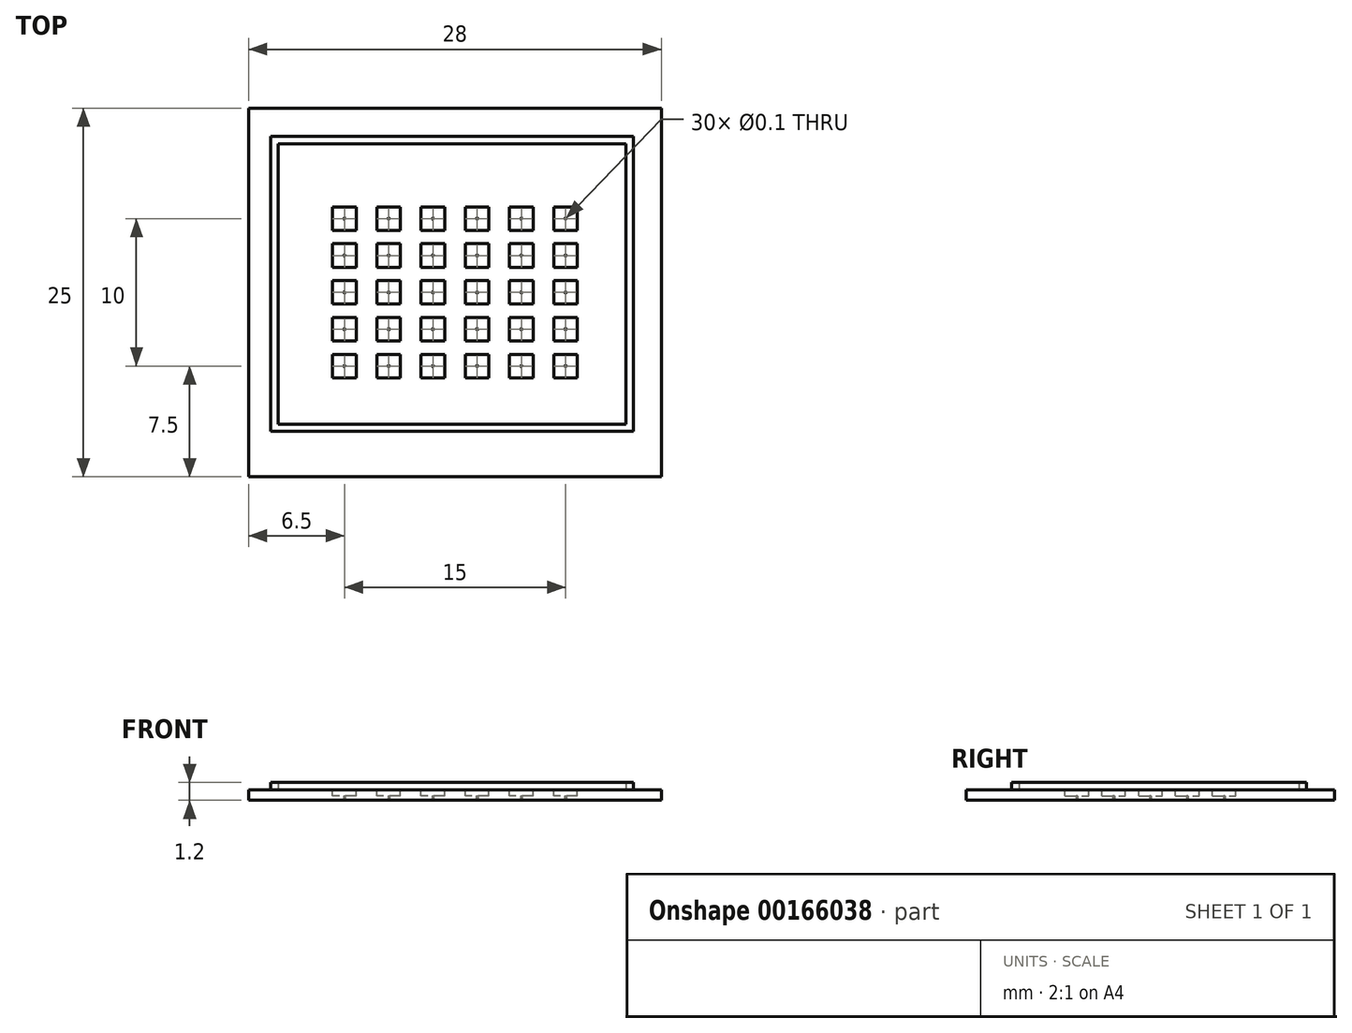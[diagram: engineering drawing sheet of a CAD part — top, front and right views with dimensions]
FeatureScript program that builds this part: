
annotation { "Feature Type Name" : "Feature", "Feature Type Description" : "" }
export const myFeature = defineFeature(function(context is Context, id is Id, definition is map)
    precondition{}
    {
        {
            var Q0;
            Q0=qCreatedBy(makeId("Top.planeOp"),FACE);
            var sketch = newSketch(context, id + "F0", { "sketchPlane" : qUnion([Q0])});
            skLineSegment(sketch, "E0.bottom", {"start": v(14, -12.5) * mm, "end": v(-14, -12.5) * mm});
            skLineSegment(sketch, "E0.top", {"start": v(14, 12.5) * mm, "end": v(-14, 12.5) * mm});
            skLineSegment(sketch, "E0.left", {"start": v(14, -12.5) * mm, "end": v(14, 12.5) * mm});
            skLineSegment(sketch, "E0.right", {"start": v(-14, -12.5) * mm, "end": v(-14, 12.5) * mm});
            skPoint(sketch, "E0.middle", {"position": v(0, 0) * mm});
            skSolve(sketch);
        }
        {
            var Q0;
            Q0=qSketchRegion(id+"F0",true);
            var Q1;
            Q1=makeQuery(id+"F0.imprint","IMPRINT",FACE,{"disambiguationData":[TD([[makeQuery(id+"F0.imprint","IMPRINT",EDGE,{"derivedFrom":sQuery(id+"F0.wireOp",EDGE,"UkhYZKIQ-UkVG-Lxvr-Lrxv-xQsFVOTcTfzZ.bottom")}),-1.0]])]});
            extrude(context, id + "F1", {"entities" : qUnion([Q0, Q1]), "oppositeDirection" : true, "depth" : 0.7 * mm});
        }
        {
            var Q0;
            Q0=makeQuery(id+"F1.opExtrude","CAP_FACE",FACE,{"disambiguationData":[OSD([sQuery(id+"F0.wireOp",EDGE,"E0.bottom"),sQuery(id+"F0.wireOp",EDGE,"E0.top"),sQuery(id+"F0.wireOp",EDGE,"E0.left"),sQuery(id+"F0.wireOp",EDGE,"E0.right")])],"isStart":true});
            var sketch = newSketch(context, id + "F2", { "sketchPlane" : qUnion([Q0])});
            skPoint(sketch, "E1.middle", {"position": v(0, 0) * mm});
            skLineSegment(sketch, "E2.bottom", {"start": v(14, -12.5) * mm, "end": v(-14, -12.5) * mm});
            skLineSegment(sketch, "E2.top", {"start": v(14, 12.5) * mm, "end": v(-14, 12.5) * mm});
            skLineSegment(sketch, "E2.left", {"start": v(14, -12.5) * mm, "end": v(14, 12.5) * mm});
            skLineSegment(sketch, "E2.right", {"start": v(-14, -12.5) * mm, "end": v(-14, 12.5) * mm});
            skPoint(sketch, "E3", {"position": v(-12.5, 10.57) * mm});
            skPoint(sketch, "E4", {"position": v(12.1, 10.57) * mm});
            skPoint(sketch, "E5", {"position": v(12.1, -9.43) * mm});
            skPoint(sketch, "E6", {"position": v(-12.5, -9.43) * mm});
            skLineSegment(sketch, "E7", {"start": v(-12.5, 10.57) * mm, "end": v(12.1, 10.57) * mm});
            skLineSegment(sketch, "E8", {"start": v(12.1, 10.57) * mm, "end": v(12.1, -9.43) * mm});
            skLineSegment(sketch, "E9", {"start": v(12.1, -9.43) * mm, "end": v(-12.5, -9.43) * mm});
            skLineSegment(sketch, "E10", {"start": v(-12.5, -9.43) * mm, "end": v(-12.5, 10.57) * mm});
            skLineSegment(sketch, "E11.0", {"start": v(-12, 10.07) * mm, "end": v(11.6, 10.07) * mm});
            skLineSegment(sketch, "E11.1", {"start": v(-12, -8.93) * mm, "end": v(-12, 10.07) * mm});
            skLineSegment(sketch, "E11.2", {"start": v(11.6, -8.93) * mm, "end": v(-12, -8.93) * mm});
            skLineSegment(sketch, "E11.3", {"start": v(11.6, 10.07) * mm, "end": v(11.6, -8.93) * mm});
            skLineSegment(sketch, "E12.0", {"start": v(-13, 11.07) * mm, "end": v(12.6, 11.07) * mm});
            skLineSegment(sketch, "E12.1", {"start": v(-13, -9.93) * mm, "end": v(-13, 11.07) * mm});
            skLineSegment(sketch, "E12.2", {"start": v(12.6, -9.93) * mm, "end": v(-13, -9.93) * mm});
            skLineSegment(sketch, "E12.3", {"start": v(12.6, 11.07) * mm, "end": v(12.6, -9.93) * mm});
            skSolve(sketch);
        }
        {
            var Q0;
            Q0=makeQuery(id+"FLxWal6u9J4FSth_1.boolean.opBoolean","SPLIT",FACE,{"disambiguationData":[TD([makeQuery(id+"FLxWal6u9J4FSth_1.opExtrude","SWEPT_FACE",FACE,{"disambiguationData":[OSD([sQuery(id+"F2.wireOp",EDGE,"E1.bottom")])]})])],"derivedFrom":makeQuery(id+"F1.opExtrude","CAP_FACE",FACE,{"disambiguationData":[OSD([sQuery(id+"F0.wireOp",EDGE,"E0.bottom"),sQuery(id+"F0.wireOp",EDGE,"E0.top"),sQuery(id+"F0.wireOp",EDGE,"E0.left"),sQuery(id+"F0.wireOp",EDGE,"E0.right")])],"isStart":true})});
            var sketch = newSketch(context, id + "F3", { "sketchPlane" : qUnion([Q0])});
            skPoint(sketch, "E13.middle", {"position": v(0, 0) * mm});
            skPoint(sketch, "E14", {"position": v(-7.5, 5) * mm});
            skPoint(sketch, "E15", {"position": v(-4.5, 5) * mm});
            skPoint(sketch, "E16", {"position": v(-1.5, 5) * mm});
            skPoint(sketch, "E17", {"position": v(1.5, 5) * mm});
            skPoint(sketch, "E18", {"position": v(4.5, 5) * mm});
            skPoint(sketch, "E19", {"position": v(7.5, 5) * mm});
            skPoint(sketch, "E20", {"position": v(-7.5, 2.5) * mm});
            skPoint(sketch, "E21", {"position": v(-4.5, 2.5) * mm});
            skPoint(sketch, "E22", {"position": v(-1.5, 2.5) * mm});
            skPoint(sketch, "E23", {"position": v(1.5, 2.5) * mm});
            skPoint(sketch, "E24", {"position": v(4.5, 2.5) * mm});
            skPoint(sketch, "E25", {"position": v(7.5, 2.5) * mm});
            skPoint(sketch, "E26", {"position": v(-7.5, 0) * mm});
            skPoint(sketch, "E27", {"position": v(-4.5, 0) * mm});
            skPoint(sketch, "E28", {"position": v(-1.5, 0) * mm});
            skPoint(sketch, "E29", {"position": v(1.5, 0) * mm});
            skPoint(sketch, "E30", {"position": v(4.5, 0) * mm});
            skPoint(sketch, "E31", {"position": v(7.5, 0) * mm});
            skPoint(sketch, "E32", {"position": v(-7.5, -2.5) * mm});
            skPoint(sketch, "E33", {"position": v(-4.5, -2.5) * mm});
            skPoint(sketch, "E34", {"position": v(-1.5, -2.5) * mm});
            skPoint(sketch, "E35", {"position": v(1.5, -2.5) * mm});
            skPoint(sketch, "E36", {"position": v(4.5, -2.5) * mm});
            skPoint(sketch, "E37", {"position": v(7.5, -2.5) * mm});
            skPoint(sketch, "E38", {"position": v(-7.5, -5) * mm});
            skPoint(sketch, "E39", {"position": v(-4.5, -5) * mm});
            skPoint(sketch, "E40", {"position": v(-1.5, -5) * mm});
            skPoint(sketch, "E41", {"position": v(1.5, -5) * mm});
            skPoint(sketch, "E42", {"position": v(4.5, -5) * mm});
            skPoint(sketch, "E43", {"position": v(7.5, -5) * mm});
            skLineSegment(sketch, "E44.bottom", {"start": v(-6.7, 4.2) * mm, "end": v(-8.3, 4.2) * mm});
            skLineSegment(sketch, "E44.top", {"start": v(-6.7, 5.8) * mm, "end": v(-8.3, 5.8) * mm});
            skLineSegment(sketch, "E44.left", {"start": v(-6.7, 4.2) * mm, "end": v(-6.7, 5.8) * mm});
            skLineSegment(sketch, "E44.right", {"start": v(-8.3, 4.2) * mm, "end": v(-8.3, 5.8) * mm});
            skLineSegment(sketch, "E45.bottom", {"start": v(-3.7, 4.2) * mm, "end": v(-5.3, 4.2) * mm});
            skLineSegment(sketch, "E45.top", {"start": v(-3.7, 5.8) * mm, "end": v(-5.3, 5.8) * mm});
            skLineSegment(sketch, "E45.left", {"start": v(-3.7, 4.2) * mm, "end": v(-3.7, 5.8) * mm});
            skLineSegment(sketch, "E45.right", {"start": v(-5.3, 4.2) * mm, "end": v(-5.3, 5.8) * mm});
            skLineSegment(sketch, "E46.bottom", {"start": v(-0.7, 4.2) * mm, "end": v(-2.3, 4.2) * mm});
            skLineSegment(sketch, "E46.top", {"start": v(-0.7, 5.8) * mm, "end": v(-2.3, 5.8) * mm});
            skLineSegment(sketch, "E46.left", {"start": v(-0.7, 4.2) * mm, "end": v(-0.7, 5.8) * mm});
            skLineSegment(sketch, "E46.right", {"start": v(-2.3, 4.2) * mm, "end": v(-2.3, 5.8) * mm});
            skLineSegment(sketch, "E47.bottom", {"start": v(2.3, 4.2) * mm, "end": v(0.7, 4.2) * mm});
            skLineSegment(sketch, "E47.top", {"start": v(2.3, 5.8) * mm, "end": v(0.7, 5.8) * mm});
            skLineSegment(sketch, "E47.left", {"start": v(2.3, 4.2) * mm, "end": v(2.3, 5.8) * mm});
            skLineSegment(sketch, "E47.right", {"start": v(0.7, 4.2) * mm, "end": v(0.7, 5.8) * mm});
            skLineSegment(sketch, "E48.bottom", {"start": v(5.3, 4.2) * mm, "end": v(3.7, 4.2) * mm});
            skLineSegment(sketch, "E48.top", {"start": v(5.3, 5.8) * mm, "end": v(3.7, 5.8) * mm});
            skLineSegment(sketch, "E48.left", {"start": v(5.3, 4.2) * mm, "end": v(5.3, 5.8) * mm});
            skLineSegment(sketch, "E48.right", {"start": v(3.7, 4.2) * mm, "end": v(3.7, 5.8) * mm});
            skLineSegment(sketch, "E49.bottom", {"start": v(8.3, 4.2) * mm, "end": v(6.7, 4.2) * mm});
            skLineSegment(sketch, "E49.top", {"start": v(8.3, 5.8) * mm, "end": v(6.7, 5.8) * mm});
            skLineSegment(sketch, "E49.left", {"start": v(8.3, 4.2) * mm, "end": v(8.3, 5.8) * mm});
            skLineSegment(sketch, "E49.right", {"start": v(6.7, 4.2) * mm, "end": v(6.7, 5.8) * mm});
            skLineSegment(sketch, "E50.bottom", {"start": v(-6.7, 1.7) * mm, "end": v(-8.3, 1.7) * mm});
            skLineSegment(sketch, "E50.top", {"start": v(-6.7, 3.3) * mm, "end": v(-8.3, 3.3) * mm});
            skLineSegment(sketch, "E50.left", {"start": v(-6.7, 1.7) * mm, "end": v(-6.7, 3.3) * mm});
            skLineSegment(sketch, "E50.right", {"start": v(-8.3, 1.7) * mm, "end": v(-8.3, 3.3) * mm});
            skLineSegment(sketch, "E51.bottom", {"start": v(-3.7, 1.7) * mm, "end": v(-5.3, 1.7) * mm});
            skLineSegment(sketch, "E51.top", {"start": v(-3.7, 3.3) * mm, "end": v(-5.3, 3.3) * mm});
            skLineSegment(sketch, "E51.left", {"start": v(-3.7, 1.7) * mm, "end": v(-3.7, 3.3) * mm});
            skLineSegment(sketch, "E51.right", {"start": v(-5.3, 1.7) * mm, "end": v(-5.3, 3.3) * mm});
            skLineSegment(sketch, "E52.bottom", {"start": v(-0.7, 1.7) * mm, "end": v(-2.3, 1.7) * mm});
            skLineSegment(sketch, "E52.top", {"start": v(-0.7, 3.3) * mm, "end": v(-2.3, 3.3) * mm});
            skLineSegment(sketch, "E52.left", {"start": v(-0.7, 1.7) * mm, "end": v(-0.7, 3.3) * mm});
            skLineSegment(sketch, "E52.right", {"start": v(-2.3, 1.7) * mm, "end": v(-2.3, 3.3) * mm});
            skLineSegment(sketch, "E53.bottom", {"start": v(2.3, 1.7) * mm, "end": v(0.7, 1.7) * mm});
            skLineSegment(sketch, "E53.top", {"start": v(2.3, 3.3) * mm, "end": v(0.7, 3.3) * mm});
            skLineSegment(sketch, "E53.left", {"start": v(2.3, 1.7) * mm, "end": v(2.3, 3.3) * mm});
            skLineSegment(sketch, "E53.right", {"start": v(0.7, 1.7) * mm, "end": v(0.7, 3.3) * mm});
            skLineSegment(sketch, "E54.bottom", {"start": v(5.3, 1.7) * mm, "end": v(3.7, 1.7) * mm});
            skLineSegment(sketch, "E54.top", {"start": v(5.3, 3.3) * mm, "end": v(3.7, 3.3) * mm});
            skLineSegment(sketch, "E54.left", {"start": v(5.3, 1.7) * mm, "end": v(5.3, 3.3) * mm});
            skLineSegment(sketch, "E54.right", {"start": v(3.7, 1.7) * mm, "end": v(3.7, 3.3) * mm});
            skLineSegment(sketch, "E55.bottom", {"start": v(8.3, 1.7) * mm, "end": v(6.7, 1.7) * mm});
            skLineSegment(sketch, "E55.top", {"start": v(8.3, 3.3) * mm, "end": v(6.7, 3.3) * mm});
            skLineSegment(sketch, "E55.left", {"start": v(8.3, 1.7) * mm, "end": v(8.3, 3.3) * mm});
            skLineSegment(sketch, "E55.right", {"start": v(6.7, 1.7) * mm, "end": v(6.7, 3.3) * mm});
            skLineSegment(sketch, "E56.bottom", {"start": v(-6.7, -0.8) * mm, "end": v(-8.3, -0.8) * mm});
            skLineSegment(sketch, "E56.top", {"start": v(-6.7, 0.8) * mm, "end": v(-8.3, 0.8) * mm});
            skLineSegment(sketch, "E56.left", {"start": v(-6.7, -0.8) * mm, "end": v(-6.7, 0.8) * mm});
            skLineSegment(sketch, "E56.right", {"start": v(-8.3, -0.8) * mm, "end": v(-8.3, 0.8) * mm});
            skLineSegment(sketch, "E57.bottom", {"start": v(-3.7, -0.8) * mm, "end": v(-5.3, -0.8) * mm});
            skLineSegment(sketch, "E57.top", {"start": v(-3.7, 0.8) * mm, "end": v(-5.3, 0.8) * mm});
            skLineSegment(sketch, "E57.left", {"start": v(-3.7, -0.8) * mm, "end": v(-3.7, 0.8) * mm});
            skLineSegment(sketch, "E57.right", {"start": v(-5.3, -0.8) * mm, "end": v(-5.3, 0.8) * mm});
            skLineSegment(sketch, "E58.bottom", {"start": v(-0.7, -0.8) * mm, "end": v(-2.3, -0.8) * mm});
            skLineSegment(sketch, "E58.top", {"start": v(-0.7, 0.8) * mm, "end": v(-2.3, 0.8) * mm});
            skLineSegment(sketch, "E58.left", {"start": v(-0.7, -0.8) * mm, "end": v(-0.7, 0.8) * mm});
            skLineSegment(sketch, "E58.right", {"start": v(-2.3, -0.8) * mm, "end": v(-2.3, 0.8) * mm});
            skLineSegment(sketch, "E59.bottom", {"start": v(2.3, -0.8) * mm, "end": v(0.7, -0.8) * mm});
            skLineSegment(sketch, "E59.top", {"start": v(2.3, 0.8) * mm, "end": v(0.7, 0.8) * mm});
            skLineSegment(sketch, "E59.left", {"start": v(2.3, -0.8) * mm, "end": v(2.3, 0.8) * mm});
            skLineSegment(sketch, "E59.right", {"start": v(0.7, -0.8) * mm, "end": v(0.7, 0.8) * mm});
            skLineSegment(sketch, "E60.bottom", {"start": v(5.3, -0.8) * mm, "end": v(3.7, -0.8) * mm});
            skLineSegment(sketch, "E60.top", {"start": v(5.3, 0.8) * mm, "end": v(3.7, 0.8) * mm});
            skLineSegment(sketch, "E60.left", {"start": v(5.3, -0.8) * mm, "end": v(5.3, 0.8) * mm});
            skLineSegment(sketch, "E60.right", {"start": v(3.7, -0.8) * mm, "end": v(3.7, 0.8) * mm});
            skLineSegment(sketch, "E61.bottom", {"start": v(8.3, -0.8) * mm, "end": v(6.7, -0.8) * mm});
            skLineSegment(sketch, "E61.top", {"start": v(8.3, 0.8) * mm, "end": v(6.7, 0.8) * mm});
            skLineSegment(sketch, "E61.left", {"start": v(8.3, -0.8) * mm, "end": v(8.3, 0.8) * mm});
            skLineSegment(sketch, "E61.right", {"start": v(6.7, -0.8) * mm, "end": v(6.7, 0.8) * mm});
            skLineSegment(sketch, "E62.bottom", {"start": v(-6.7, -3.3) * mm, "end": v(-8.3, -3.3) * mm});
            skLineSegment(sketch, "E62.top", {"start": v(-6.7, -1.7) * mm, "end": v(-8.3, -1.7) * mm});
            skLineSegment(sketch, "E62.left", {"start": v(-6.7, -3.3) * mm, "end": v(-6.7, -1.7) * mm});
            skLineSegment(sketch, "E62.right", {"start": v(-8.3, -3.3) * mm, "end": v(-8.3, -1.7) * mm});
            skLineSegment(sketch, "E63.bottom", {"start": v(-3.7, -3.3) * mm, "end": v(-5.3, -3.3) * mm});
            skLineSegment(sketch, "E63.top", {"start": v(-3.7, -1.7) * mm, "end": v(-5.3, -1.7) * mm});
            skLineSegment(sketch, "E63.left", {"start": v(-3.7, -3.3) * mm, "end": v(-3.7, -1.7) * mm});
            skLineSegment(sketch, "E63.right", {"start": v(-5.3, -3.3) * mm, "end": v(-5.3, -1.7) * mm});
            skLineSegment(sketch, "E64.bottom", {"start": v(-0.7, -3.3) * mm, "end": v(-2.3, -3.3) * mm});
            skLineSegment(sketch, "E64.top", {"start": v(-0.7, -1.7) * mm, "end": v(-2.3, -1.7) * mm});
            skLineSegment(sketch, "E64.left", {"start": v(-0.7, -3.3) * mm, "end": v(-0.7, -1.7) * mm});
            skLineSegment(sketch, "E64.right", {"start": v(-2.3, -3.3) * mm, "end": v(-2.3, -1.7) * mm});
            skLineSegment(sketch, "E65.bottom", {"start": v(2.3, -3.3) * mm, "end": v(0.7, -3.3) * mm});
            skLineSegment(sketch, "E65.top", {"start": v(2.3, -1.7) * mm, "end": v(0.7, -1.7) * mm});
            skLineSegment(sketch, "E65.left", {"start": v(2.3, -3.3) * mm, "end": v(2.3, -1.7) * mm});
            skLineSegment(sketch, "E65.right", {"start": v(0.7, -3.3) * mm, "end": v(0.7, -1.7) * mm});
            skLineSegment(sketch, "E66.bottom", {"start": v(5.3, -3.3) * mm, "end": v(3.7, -3.3) * mm});
            skLineSegment(sketch, "E66.top", {"start": v(5.3, -1.7) * mm, "end": v(3.7, -1.7) * mm});
            skLineSegment(sketch, "E66.left", {"start": v(5.3, -3.3) * mm, "end": v(5.3, -1.7) * mm});
            skLineSegment(sketch, "E66.right", {"start": v(3.7, -3.3) * mm, "end": v(3.7, -1.7) * mm});
            skLineSegment(sketch, "E67.bottom", {"start": v(8.3, -3.3) * mm, "end": v(6.7, -3.3) * mm});
            skLineSegment(sketch, "E67.top", {"start": v(8.3, -1.7) * mm, "end": v(6.7, -1.7) * mm});
            skLineSegment(sketch, "E67.left", {"start": v(8.3, -3.3) * mm, "end": v(8.3, -1.7) * mm});
            skLineSegment(sketch, "E67.right", {"start": v(6.7, -3.3) * mm, "end": v(6.7, -1.7) * mm});
            skLineSegment(sketch, "E68.bottom", {"start": v(-6.7, -5.8) * mm, "end": v(-8.3, -5.8) * mm});
            skLineSegment(sketch, "E68.top", {"start": v(-6.7, -4.2) * mm, "end": v(-8.3, -4.2) * mm});
            skLineSegment(sketch, "E68.left", {"start": v(-6.7, -5.8) * mm, "end": v(-6.7, -4.2) * mm});
            skLineSegment(sketch, "E68.right", {"start": v(-8.3, -5.8) * mm, "end": v(-8.3, -4.2) * mm});
            skLineSegment(sketch, "E69.bottom", {"start": v(-3.7, -5.8) * mm, "end": v(-5.3, -5.8) * mm});
            skLineSegment(sketch, "E69.top", {"start": v(-3.7, -4.2) * mm, "end": v(-5.3, -4.2) * mm});
            skLineSegment(sketch, "E69.left", {"start": v(-3.7, -5.8) * mm, "end": v(-3.7, -4.2) * mm});
            skLineSegment(sketch, "E69.right", {"start": v(-5.3, -5.8) * mm, "end": v(-5.3, -4.2) * mm});
            skLineSegment(sketch, "E70.bottom", {"start": v(-0.7, -5.8) * mm, "end": v(-2.3, -5.8) * mm});
            skLineSegment(sketch, "E70.top", {"start": v(-0.7, -4.2) * mm, "end": v(-2.3, -4.2) * mm});
            skLineSegment(sketch, "E70.left", {"start": v(-0.7, -5.8) * mm, "end": v(-0.7, -4.2) * mm});
            skLineSegment(sketch, "E70.right", {"start": v(-2.3, -5.8) * mm, "end": v(-2.3, -4.2) * mm});
            skLineSegment(sketch, "E71.bottom", {"start": v(2.3, -5.8) * mm, "end": v(0.7, -5.8) * mm});
            skLineSegment(sketch, "E71.top", {"start": v(2.3, -4.2) * mm, "end": v(0.7, -4.2) * mm});
            skLineSegment(sketch, "E71.left", {"start": v(2.3, -5.8) * mm, "end": v(2.3, -4.2) * mm});
            skLineSegment(sketch, "E71.right", {"start": v(0.7, -5.8) * mm, "end": v(0.7, -4.2) * mm});
            skLineSegment(sketch, "E72.bottom", {"start": v(5.3, -5.8) * mm, "end": v(3.7, -5.8) * mm});
            skLineSegment(sketch, "E72.top", {"start": v(5.3, -4.2) * mm, "end": v(3.7, -4.2) * mm});
            skLineSegment(sketch, "E72.left", {"start": v(5.3, -5.8) * mm, "end": v(5.3, -4.2) * mm});
            skLineSegment(sketch, "E72.right", {"start": v(3.7, -5.8) * mm, "end": v(3.7, -4.2) * mm});
            skLineSegment(sketch, "E73.bottom", {"start": v(8.3, -5.8) * mm, "end": v(6.7, -5.8) * mm});
            skLineSegment(sketch, "E73.top", {"start": v(8.3, -4.2) * mm, "end": v(6.7, -4.2) * mm});
            skLineSegment(sketch, "E73.left", {"start": v(8.3, -5.8) * mm, "end": v(8.3, -4.2) * mm});
            skLineSegment(sketch, "E73.right", {"start": v(6.7, -5.8) * mm, "end": v(6.7, -4.2) * mm});
            skSolve(sketch);
        }
        {
            var Q0;
            Q0 = qSketchRegion(id + "F3", true);
            extrude(context, id + "F4", {"entities" : qUnion([Q0]), "operationType" : NewBodyOperationType.REMOVE, "oppositeDirection" : true, "depth" : 0.4 * mm});
        }
        {
            var Q0;
            Q0=makeQuery(id+"F4.boolean.opBoolean","COPY",FACE,{"derivedFrom":makeQuery(id+"F4.opExtrude","CAP_FACE",FACE,{"disambiguationData":[OSD([sQuery(id+"F3.wireOp",EDGE,"E44.bottom"),sQuery(id+"F3.wireOp",EDGE,"E44.top"),sQuery(id+"F3.wireOp",EDGE,"E44.left"),sQuery(id+"F3.wireOp",EDGE,"E44.right")])],"isStart":false})});
            var sketch = newSketch(context, id + "F5", { "sketchPlane" : qUnion([Q0])});
            skPoint(sketch, "E74", {"position": v(-7.5, 5) * mm});
            skSolve(sketch);
        }
        {
            var Q0;
            Q0=sQuery(id+"F5.wireOp",VERTEX,"E74");
            var Q1;
            Q1=makeQuery(id+"F1.opExtrude","SWEPT_BODY",BODY,{"disambiguationData":[OSD([sQuery(id+"F0.wireOp",EDGE,"E0.bottom"),sQuery(id+"F0.wireOp",EDGE,"E0.top"),sQuery(id+"F0.wireOp",EDGE,"E0.left"),sQuery(id+"F0.wireOp",EDGE,"E0.right")])]});
            hole(context, id + "F6", {"style" : HoleStyle.SIMPLE, "endStyle" : HoleEndStyle.THROUGH, "holeDiameter" : 0.1 * mm, "startFromSketch" : true, "locations" : qUnion([Q0]), "scope" : qUnion([Q1]), "isTappedThrough" : true});
        }
        {
            var Q0;
            Q0=makeQuery(id+"F4.boolean.opBoolean","COPY",FACE,{"derivedFrom":makeQuery(id+"F4.opExtrude","CAP_FACE",FACE,{"disambiguationData":[OSD([sQuery(id+"F3.wireOp",EDGE,"E45.bottom"),sQuery(id+"F3.wireOp",EDGE,"E45.top"),sQuery(id+"F3.wireOp",EDGE,"E45.left"),sQuery(id+"F3.wireOp",EDGE,"E45.right")])],"isStart":false})});
            var sketch = newSketch(context, id + "F7", { "sketchPlane" : qUnion([Q0])});
            skPoint(sketch, "E75", {"position": v(-4.5, 5) * mm});
            skSolve(sketch);
        }
        {
            var Q0;
            Q0=sQuery(id+"F7.wireOp",VERTEX,"E75");
            var Q1;
            Q1=makeQuery(id+"F1.opExtrude","SWEPT_BODY",BODY,{"disambiguationData":[OSD([sQuery(id+"F0.wireOp",EDGE,"E0.bottom"),sQuery(id+"F0.wireOp",EDGE,"E0.top"),sQuery(id+"F0.wireOp",EDGE,"E0.left"),sQuery(id+"F0.wireOp",EDGE,"E0.right")])]});
            hole(context, id + "F8", {"style" : HoleStyle.SIMPLE, "endStyle" : HoleEndStyle.THROUGH, "holeDiameter" : 0.1 * mm, "startFromSketch" : true, "locations" : qUnion([Q0]), "scope" : qUnion([Q1]), "isTappedThrough" : true});
        }
        {
            var Q0;
            Q0=makeQuery(id+"F4.boolean.opBoolean","COPY",FACE,{"derivedFrom":makeQuery(id+"F4.opExtrude","CAP_FACE",FACE,{"disambiguationData":[OSD([sQuery(id+"F3.wireOp",EDGE,"E46.bottom"),sQuery(id+"F3.wireOp",EDGE,"E46.top"),sQuery(id+"F3.wireOp",EDGE,"E46.left"),sQuery(id+"F3.wireOp",EDGE,"E46.right")])],"isStart":false})});
            var sketch = newSketch(context, id + "F9", { "sketchPlane" : qUnion([Q0])});
            skPoint(sketch, "E76", {"position": v(-1.5, 5) * mm});
            skSolve(sketch);
        }
        {
            var Q0;
            Q0=sQuery(id+"F9.wireOp",VERTEX,"E76");
            var Q1;
            Q1=makeQuery(id+"F1.opExtrude","SWEPT_BODY",BODY,{"disambiguationData":[OSD([sQuery(id+"F0.wireOp",EDGE,"E0.bottom"),sQuery(id+"F0.wireOp",EDGE,"E0.top"),sQuery(id+"F0.wireOp",EDGE,"E0.left"),sQuery(id+"F0.wireOp",EDGE,"E0.right")])]});
            hole(context, id + "F10", {"style" : HoleStyle.SIMPLE, "endStyle" : HoleEndStyle.THROUGH, "holeDiameter" : 0.1 * mm, "startFromSketch" : true, "locations" : qUnion([Q0]), "scope" : qUnion([Q1]), "isTappedThrough" : true});
        }
        {
            var Q0;
            Q0=makeQuery(id+"F4.boolean.opBoolean","COPY",FACE,{"derivedFrom":makeQuery(id+"F4.opExtrude","CAP_FACE",FACE,{"disambiguationData":[OSD([sQuery(id+"F3.wireOp",EDGE,"E47.bottom"),sQuery(id+"F3.wireOp",EDGE,"E47.top"),sQuery(id+"F3.wireOp",EDGE,"E47.left"),sQuery(id+"F3.wireOp",EDGE,"E47.right")])],"isStart":false})});
            var sketch = newSketch(context, id + "F11", { "sketchPlane" : qUnion([Q0])});
            skPoint(sketch, "E77", {"position": v(1.5, 5) * mm});
            skSolve(sketch);
        }
        {
            var Q0;
            Q0=sQuery(id+"F11.wireOp",VERTEX,"E77");
            var Q1;
            Q1=makeQuery(id+"F1.opExtrude","SWEPT_BODY",BODY,{"disambiguationData":[OSD([sQuery(id+"F0.wireOp",EDGE,"E0.bottom"),sQuery(id+"F0.wireOp",EDGE,"E0.top"),sQuery(id+"F0.wireOp",EDGE,"E0.left"),sQuery(id+"F0.wireOp",EDGE,"E0.right")])]});
            hole(context, id + "F12", {"style" : HoleStyle.SIMPLE, "endStyle" : HoleEndStyle.THROUGH, "holeDiameter" : 0.1 * mm, "startFromSketch" : true, "locations" : qUnion([Q0]), "scope" : qUnion([Q1]), "isTappedThrough" : true});
        }
        {
            var Q0;
            Q0=makeQuery(id+"F4.boolean.opBoolean","COPY",FACE,{"derivedFrom":makeQuery(id+"F4.opExtrude","CAP_FACE",FACE,{"disambiguationData":[OSD([sQuery(id+"F3.wireOp",EDGE,"E48.bottom"),sQuery(id+"F3.wireOp",EDGE,"E48.top"),sQuery(id+"F3.wireOp",EDGE,"E48.left"),sQuery(id+"F3.wireOp",EDGE,"E48.right")])],"isStart":false})});
            var sketch = newSketch(context, id + "F13", { "sketchPlane" : qUnion([Q0])});
            skPoint(sketch, "E78", {"position": v(4.5, 5) * mm});
            skSolve(sketch);
        }
        {
            var Q0;
            Q0=sQuery(id+"F13.wireOp",VERTEX,"E78");
            var Q1;
            Q1=makeQuery(id+"F1.opExtrude","SWEPT_BODY",BODY,{"disambiguationData":[OSD([sQuery(id+"F0.wireOp",EDGE,"E0.bottom"),sQuery(id+"F0.wireOp",EDGE,"E0.top"),sQuery(id+"F0.wireOp",EDGE,"E0.left"),sQuery(id+"F0.wireOp",EDGE,"E0.right")])]});
            hole(context, id + "F14", {"style" : HoleStyle.SIMPLE, "endStyle" : HoleEndStyle.THROUGH, "holeDiameter" : 0.1 * mm, "startFromSketch" : true, "locations" : qUnion([Q0]), "scope" : qUnion([Q1]), "isTappedThrough" : true});
        }
        {
            var Q0;
            Q0=makeQuery(id+"F4.boolean.opBoolean","COPY",FACE,{"derivedFrom":makeQuery(id+"F4.opExtrude","CAP_FACE",FACE,{"disambiguationData":[OSD([sQuery(id+"F3.wireOp",EDGE,"E49.bottom"),sQuery(id+"F3.wireOp",EDGE,"E49.top"),sQuery(id+"F3.wireOp",EDGE,"E49.left"),sQuery(id+"F3.wireOp",EDGE,"E49.right")])],"isStart":false})});
            var sketch = newSketch(context, id + "F15", { "sketchPlane" : qUnion([Q0])});
            skPoint(sketch, "E79", {"position": v(7.5, 5) * mm});
            skSolve(sketch);
        }
        {
            var Q0;
            Q0=sQuery(id+"F15.wireOp",VERTEX,"E79");
            var Q1;
            Q1=makeQuery(id+"F1.opExtrude","SWEPT_BODY",BODY,{"disambiguationData":[OSD([sQuery(id+"F0.wireOp",EDGE,"E0.bottom"),sQuery(id+"F0.wireOp",EDGE,"E0.top"),sQuery(id+"F0.wireOp",EDGE,"E0.left"),sQuery(id+"F0.wireOp",EDGE,"E0.right")])]});
            hole(context, id + "F16", {"style" : HoleStyle.SIMPLE, "endStyle" : HoleEndStyle.THROUGH, "holeDiameter" : 0.1 * mm, "startFromSketch" : true, "locations" : qUnion([Q0]), "scope" : qUnion([Q1]), "isTappedThrough" : true});
        }
        {
            var Q0;
            Q0=makeQuery(id+"F4.boolean.opBoolean","COPY",FACE,{"derivedFrom":makeQuery(id+"F4.opExtrude","CAP_FACE",FACE,{"disambiguationData":[OSD([sQuery(id+"F3.wireOp",EDGE,"E55.bottom"),sQuery(id+"F3.wireOp",EDGE,"E55.top"),sQuery(id+"F3.wireOp",EDGE,"E55.left"),sQuery(id+"F3.wireOp",EDGE,"E55.right")])],"isStart":false})});
            var sketch = newSketch(context, id + "F17", { "sketchPlane" : qUnion([Q0])});
            skPoint(sketch, "E80", {"position": v(7.5, 2.5) * mm});
            skSolve(sketch);
        }
        {
            var Q0;
            Q0=sQuery(id+"F17.wireOp",VERTEX,"E80");
            var Q1;
            Q1=makeQuery(id+"F1.opExtrude","SWEPT_BODY",BODY,{"disambiguationData":[OSD([sQuery(id+"F0.wireOp",EDGE,"E0.bottom"),sQuery(id+"F0.wireOp",EDGE,"E0.top"),sQuery(id+"F0.wireOp",EDGE,"E0.left"),sQuery(id+"F0.wireOp",EDGE,"E0.right")])]});
            hole(context, id + "F18", {"style" : HoleStyle.SIMPLE, "endStyle" : HoleEndStyle.THROUGH, "holeDiameter" : 0.1 * mm, "startFromSketch" : true, "locations" : qUnion([Q0]), "scope" : qUnion([Q1]), "isTappedThrough" : true});
        }
        {
            var Q0;
            Q0=makeQuery(id+"F4.boolean.opBoolean","COPY",FACE,{"derivedFrom":makeQuery(id+"F4.opExtrude","CAP_FACE",FACE,{"disambiguationData":[OSD([sQuery(id+"F3.wireOp",EDGE,"E54.bottom"),sQuery(id+"F3.wireOp",EDGE,"E54.top"),sQuery(id+"F3.wireOp",EDGE,"E54.left"),sQuery(id+"F3.wireOp",EDGE,"E54.right")])],"isStart":false})});
            var sketch = newSketch(context, id + "F19", { "sketchPlane" : qUnion([Q0])});
            skPoint(sketch, "E81", {"position": v(4.5, 2.5) * mm});
            skSolve(sketch);
        }
        {
            var Q0;
            Q0=sQuery(id+"F19.wireOp",VERTEX,"E81");
            var Q1;
            Q1=makeQuery(id+"F1.opExtrude","SWEPT_BODY",BODY,{"disambiguationData":[OSD([sQuery(id+"F0.wireOp",EDGE,"E0.bottom"),sQuery(id+"F0.wireOp",EDGE,"E0.top"),sQuery(id+"F0.wireOp",EDGE,"E0.left"),sQuery(id+"F0.wireOp",EDGE,"E0.right")])]});
            hole(context, id + "F20", {"style" : HoleStyle.SIMPLE, "endStyle" : HoleEndStyle.THROUGH, "holeDiameter" : 0.1 * mm, "startFromSketch" : true, "locations" : qUnion([Q0]), "scope" : qUnion([Q1]), "isTappedThrough" : true});
        }
        {
            var Q0;
            Q0=makeQuery(id+"F4.boolean.opBoolean","COPY",FACE,{"derivedFrom":makeQuery(id+"F4.opExtrude","CAP_FACE",FACE,{"disambiguationData":[OSD([sQuery(id+"F3.wireOp",EDGE,"E53.bottom"),sQuery(id+"F3.wireOp",EDGE,"E53.top"),sQuery(id+"F3.wireOp",EDGE,"E53.left"),sQuery(id+"F3.wireOp",EDGE,"E53.right")])],"isStart":false})});
            var sketch = newSketch(context, id + "F21", { "sketchPlane" : qUnion([Q0])});
            skPoint(sketch, "E82", {"position": v(1.5, 2.5) * mm});
            skSolve(sketch);
        }
        {
            var Q0;
            Q0=sQuery(id+"F21.wireOp",VERTEX,"E82");
            var Q1;
            Q1=makeQuery(id+"F1.opExtrude","SWEPT_BODY",BODY,{"disambiguationData":[OSD([sQuery(id+"F0.wireOp",EDGE,"E0.bottom"),sQuery(id+"F0.wireOp",EDGE,"E0.top"),sQuery(id+"F0.wireOp",EDGE,"E0.left"),sQuery(id+"F0.wireOp",EDGE,"E0.right")])]});
            hole(context, id + "F22", {"style" : HoleStyle.SIMPLE, "endStyle" : HoleEndStyle.THROUGH, "holeDiameter" : 0.1 * mm, "startFromSketch" : true, "locations" : qUnion([Q0]), "scope" : qUnion([Q1]), "isTappedThrough" : true});
        }
        {
            var Q0;
            Q0=makeQuery(id+"F4.boolean.opBoolean","COPY",FACE,{"derivedFrom":makeQuery(id+"F4.opExtrude","CAP_FACE",FACE,{"disambiguationData":[OSD([sQuery(id+"F3.wireOp",EDGE,"E52.bottom"),sQuery(id+"F3.wireOp",EDGE,"E52.top"),sQuery(id+"F3.wireOp",EDGE,"E52.left"),sQuery(id+"F3.wireOp",EDGE,"E52.right")])],"isStart":false})});
            var sketch = newSketch(context, id + "F23", { "sketchPlane" : qUnion([Q0])});
            skPoint(sketch, "E83", {"position": v(-1.5, 2.5) * mm});
            skSolve(sketch);
        }
        {
            var Q0;
            Q0=sQuery(id+"F23.wireOp",VERTEX,"E83");
            var Q1;
            Q1=makeQuery(id+"F1.opExtrude","SWEPT_BODY",BODY,{"disambiguationData":[OSD([sQuery(id+"F0.wireOp",EDGE,"E0.bottom"),sQuery(id+"F0.wireOp",EDGE,"E0.top"),sQuery(id+"F0.wireOp",EDGE,"E0.left"),sQuery(id+"F0.wireOp",EDGE,"E0.right")])]});
            hole(context, id + "F24", {"style" : HoleStyle.SIMPLE, "endStyle" : HoleEndStyle.THROUGH, "holeDiameter" : 0.1 * mm, "startFromSketch" : true, "locations" : qUnion([Q0]), "scope" : qUnion([Q1]), "isTappedThrough" : true});
        }
        {
            var Q0;
            Q0=makeQuery(id+"F4.boolean.opBoolean","COPY",FACE,{"derivedFrom":makeQuery(id+"F4.opExtrude","CAP_FACE",FACE,{"disambiguationData":[OSD([sQuery(id+"F3.wireOp",EDGE,"E51.bottom"),sQuery(id+"F3.wireOp",EDGE,"E51.top"),sQuery(id+"F3.wireOp",EDGE,"E51.left"),sQuery(id+"F3.wireOp",EDGE,"E51.right")])],"isStart":false})});
            var sketch = newSketch(context, id + "F25", { "sketchPlane" : qUnion([Q0])});
            skPoint(sketch, "E84", {"position": v(-4.5, 2.5) * mm});
            skSolve(sketch);
        }
        {
            var Q0;
            Q0=sQuery(id+"F25.wireOp",VERTEX,"E84");
            var Q1;
            Q1=makeQuery(id+"F1.opExtrude","SWEPT_BODY",BODY,{"disambiguationData":[OSD([sQuery(id+"F0.wireOp",EDGE,"E0.bottom"),sQuery(id+"F0.wireOp",EDGE,"E0.top"),sQuery(id+"F0.wireOp",EDGE,"E0.left"),sQuery(id+"F0.wireOp",EDGE,"E0.right")])]});
            hole(context, id + "F26", {"style" : HoleStyle.SIMPLE, "endStyle" : HoleEndStyle.THROUGH, "holeDiameter" : 0.1 * mm, "startFromSketch" : true, "locations" : qUnion([Q0]), "scope" : qUnion([Q1]), "isTappedThrough" : true});
        }
        {
            var Q0;
            Q0=makeQuery(id+"F4.boolean.opBoolean","COPY",FACE,{"derivedFrom":makeQuery(id+"F4.opExtrude","CAP_FACE",FACE,{"disambiguationData":[OSD([sQuery(id+"F3.wireOp",EDGE,"E50.bottom"),sQuery(id+"F3.wireOp",EDGE,"E50.top"),sQuery(id+"F3.wireOp",EDGE,"E50.left"),sQuery(id+"F3.wireOp",EDGE,"E50.right")])],"isStart":false})});
            var sketch = newSketch(context, id + "F27", { "sketchPlane" : qUnion([Q0])});
            skPoint(sketch, "E85", {"position": v(-7.5, 2.5) * mm});
            skSolve(sketch);
        }
        {
            var Q0;
            Q0=sQuery(id+"F27.wireOp",VERTEX,"E85");
            var Q1;
            Q1=makeQuery(id+"F1.opExtrude","SWEPT_BODY",BODY,{"disambiguationData":[OSD([sQuery(id+"F0.wireOp",EDGE,"E0.bottom"),sQuery(id+"F0.wireOp",EDGE,"E0.top"),sQuery(id+"F0.wireOp",EDGE,"E0.left"),sQuery(id+"F0.wireOp",EDGE,"E0.right")])]});
            hole(context, id + "F28", {"style" : HoleStyle.SIMPLE, "endStyle" : HoleEndStyle.THROUGH, "holeDiameter" : 0.1 * mm, "startFromSketch" : true, "locations" : qUnion([Q0]), "scope" : qUnion([Q1]), "isTappedThrough" : true});
        }
        {
            var Q0;
            Q0=makeQuery(id+"F4.boolean.opBoolean","COPY",FACE,{"derivedFrom":makeQuery(id+"F4.opExtrude","CAP_FACE",FACE,{"disambiguationData":[OSD([sQuery(id+"F3.wireOp",EDGE,"E56.bottom"),sQuery(id+"F3.wireOp",EDGE,"E56.top"),sQuery(id+"F3.wireOp",EDGE,"E56.left"),sQuery(id+"F3.wireOp",EDGE,"E56.right")])],"isStart":false})});
            var sketch = newSketch(context, id + "F29", { "sketchPlane" : qUnion([Q0])});
            skPoint(sketch, "E86", {"position": v(-7.5, 0) * mm});
            skSolve(sketch);
        }
        {
            var Q0;
            Q0=sQuery(id+"F29.wireOp",VERTEX,"E86");
            var Q1;
            Q1=makeQuery(id+"F1.opExtrude","SWEPT_BODY",BODY,{"disambiguationData":[OSD([sQuery(id+"F0.wireOp",EDGE,"E0.bottom"),sQuery(id+"F0.wireOp",EDGE,"E0.top"),sQuery(id+"F0.wireOp",EDGE,"E0.left"),sQuery(id+"F0.wireOp",EDGE,"E0.right")])]});
            hole(context, id + "F30", {"style" : HoleStyle.SIMPLE, "endStyle" : HoleEndStyle.THROUGH, "holeDiameter" : 0.1 * mm, "startFromSketch" : true, "locations" : qUnion([Q0]), "scope" : qUnion([Q1]), "isTappedThrough" : true});
        }
        {
            var Q0;
            Q0=makeQuery(id+"F4.boolean.opBoolean","COPY",FACE,{"derivedFrom":makeQuery(id+"F4.opExtrude","CAP_FACE",FACE,{"disambiguationData":[OSD([sQuery(id+"F3.wireOp",EDGE,"E57.bottom"),sQuery(id+"F3.wireOp",EDGE,"E57.top"),sQuery(id+"F3.wireOp",EDGE,"E57.left"),sQuery(id+"F3.wireOp",EDGE,"E57.right")])],"isStart":false})});
            var sketch = newSketch(context, id + "F31", { "sketchPlane" : qUnion([Q0])});
            skPoint(sketch, "E87", {"position": v(-4.5, 0) * mm});
            skSolve(sketch);
        }
        {
            var Q0;
            Q0=sQuery(id+"F31.wireOp",VERTEX,"E87");
            var Q1;
            Q1=makeQuery(id+"F1.opExtrude","SWEPT_BODY",BODY,{"disambiguationData":[OSD([sQuery(id+"F0.wireOp",EDGE,"E0.bottom"),sQuery(id+"F0.wireOp",EDGE,"E0.top"),sQuery(id+"F0.wireOp",EDGE,"E0.left"),sQuery(id+"F0.wireOp",EDGE,"E0.right")])]});
            hole(context, id + "F32", {"style" : HoleStyle.SIMPLE, "endStyle" : HoleEndStyle.THROUGH, "holeDiameter" : 0.1 * mm, "startFromSketch" : true, "locations" : qUnion([Q0]), "scope" : qUnion([Q1]), "isTappedThrough" : true});
        }
        {
            var Q0;
            Q0=makeQuery(id+"F4.boolean.opBoolean","COPY",FACE,{"derivedFrom":makeQuery(id+"F4.opExtrude","CAP_FACE",FACE,{"disambiguationData":[OSD([sQuery(id+"F3.wireOp",EDGE,"E58.bottom"),sQuery(id+"F3.wireOp",EDGE,"E58.top"),sQuery(id+"F3.wireOp",EDGE,"E58.left"),sQuery(id+"F3.wireOp",EDGE,"E58.right")])],"isStart":false})});
            var sketch = newSketch(context, id + "F33", { "sketchPlane" : qUnion([Q0])});
            skPoint(sketch, "E88", {"position": v(-1.5, 0) * mm});
            skSolve(sketch);
        }
        {
            var Q0;
            Q0=sQuery(id+"F33.wireOp",VERTEX,"E88");
            var Q1;
            Q1=makeQuery(id+"F1.opExtrude","SWEPT_BODY",BODY,{"disambiguationData":[OSD([sQuery(id+"F0.wireOp",EDGE,"E0.bottom"),sQuery(id+"F0.wireOp",EDGE,"E0.top"),sQuery(id+"F0.wireOp",EDGE,"E0.left"),sQuery(id+"F0.wireOp",EDGE,"E0.right")])]});
            hole(context, id + "F34", {"style" : HoleStyle.SIMPLE, "endStyle" : HoleEndStyle.THROUGH, "holeDiameter" : 0.1 * mm, "startFromSketch" : true, "locations" : qUnion([Q0]), "scope" : qUnion([Q1]), "isTappedThrough" : true});
        }
        {
            var Q0;
            Q0=makeQuery(id+"F4.boolean.opBoolean","COPY",FACE,{"derivedFrom":makeQuery(id+"F4.opExtrude","CAP_FACE",FACE,{"disambiguationData":[OSD([sQuery(id+"F3.wireOp",EDGE,"E59.bottom"),sQuery(id+"F3.wireOp",EDGE,"E59.top"),sQuery(id+"F3.wireOp",EDGE,"E59.left"),sQuery(id+"F3.wireOp",EDGE,"E59.right")])],"isStart":false})});
            var sketch = newSketch(context, id + "F35", { "sketchPlane" : qUnion([Q0])});
            skPoint(sketch, "E89", {"position": v(1.5, 0) * mm});
            skSolve(sketch);
        }
        {
            var Q0;
            Q0=sQuery(id+"F35.wireOp",VERTEX,"E89");
            var Q1;
            Q1=makeQuery(id+"F1.opExtrude","SWEPT_BODY",BODY,{"disambiguationData":[OSD([sQuery(id+"F0.wireOp",EDGE,"E0.bottom"),sQuery(id+"F0.wireOp",EDGE,"E0.top"),sQuery(id+"F0.wireOp",EDGE,"E0.left"),sQuery(id+"F0.wireOp",EDGE,"E0.right")])]});
            hole(context, id + "F36", {"style" : HoleStyle.SIMPLE, "endStyle" : HoleEndStyle.THROUGH, "holeDiameter" : 0.1 * mm, "startFromSketch" : true, "locations" : qUnion([Q0]), "scope" : qUnion([Q1]), "isTappedThrough" : true});
        }
        {
            var Q0;
            Q0=makeQuery(id+"F4.boolean.opBoolean","COPY",FACE,{"derivedFrom":makeQuery(id+"F4.opExtrude","CAP_FACE",FACE,{"disambiguationData":[OSD([sQuery(id+"F3.wireOp",EDGE,"E60.bottom"),sQuery(id+"F3.wireOp",EDGE,"E60.top"),sQuery(id+"F3.wireOp",EDGE,"E60.left"),sQuery(id+"F3.wireOp",EDGE,"E60.right")])],"isStart":false})});
            var sketch = newSketch(context, id + "F37", { "sketchPlane" : qUnion([Q0])});
            skPoint(sketch, "E90", {"position": v(4.5, 0) * mm});
            skSolve(sketch);
        }
        {
            var Q0;
            Q0=sQuery(id+"F37.wireOp",VERTEX,"E90");
            var Q1;
            Q1=makeQuery(id+"F1.opExtrude","SWEPT_BODY",BODY,{"disambiguationData":[OSD([sQuery(id+"F0.wireOp",EDGE,"E0.bottom"),sQuery(id+"F0.wireOp",EDGE,"E0.top"),sQuery(id+"F0.wireOp",EDGE,"E0.left"),sQuery(id+"F0.wireOp",EDGE,"E0.right")])]});
            hole(context, id + "F38", {"style" : HoleStyle.SIMPLE, "endStyle" : HoleEndStyle.THROUGH, "holeDiameter" : 0.1 * mm, "startFromSketch" : true, "locations" : qUnion([Q0]), "scope" : qUnion([Q1]), "isTappedThrough" : true});
        }
        {
            var Q0;
            Q0=makeQuery(id+"F4.boolean.opBoolean","COPY",FACE,{"derivedFrom":makeQuery(id+"F4.opExtrude","CAP_FACE",FACE,{"disambiguationData":[OSD([sQuery(id+"F3.wireOp",EDGE,"E61.bottom"),sQuery(id+"F3.wireOp",EDGE,"E61.top"),sQuery(id+"F3.wireOp",EDGE,"E61.left"),sQuery(id+"F3.wireOp",EDGE,"E61.right")])],"isStart":false})});
            var sketch = newSketch(context, id + "F39", { "sketchPlane" : qUnion([Q0])});
            skPoint(sketch, "E91", {"position": v(7.5, 0) * mm});
            skSolve(sketch);
        }
        {
            var Q0;
            Q0=sQuery(id+"F39.wireOp",VERTEX,"E91");
            var Q1;
            Q1=makeQuery(id+"F1.opExtrude","SWEPT_BODY",BODY,{"disambiguationData":[OSD([sQuery(id+"F0.wireOp",EDGE,"E0.bottom"),sQuery(id+"F0.wireOp",EDGE,"E0.top"),sQuery(id+"F0.wireOp",EDGE,"E0.left"),sQuery(id+"F0.wireOp",EDGE,"E0.right")])]});
            hole(context, id + "F40", {"style" : HoleStyle.SIMPLE, "endStyle" : HoleEndStyle.THROUGH, "holeDiameter" : 0.1 * mm, "startFromSketch" : true, "locations" : qUnion([Q0]), "scope" : qUnion([Q1]), "isTappedThrough" : true});
        }
        {
            var Q0;
            Q0=makeQuery(id+"F4.boolean.opBoolean","COPY",FACE,{"derivedFrom":makeQuery(id+"F4.opExtrude","CAP_FACE",FACE,{"disambiguationData":[OSD([sQuery(id+"F3.wireOp",EDGE,"E62.bottom"),sQuery(id+"F3.wireOp",EDGE,"E62.top"),sQuery(id+"F3.wireOp",EDGE,"E62.left"),sQuery(id+"F3.wireOp",EDGE,"E62.right")])],"isStart":false})});
            var sketch = newSketch(context, id + "F41", { "sketchPlane" : qUnion([Q0])});
            skPoint(sketch, "E92", {"position": v(-7.5, -2.5) * mm});
            skSolve(sketch);
        }
        {
            var Q0;
            Q0=sQuery(id+"F41.wireOp",VERTEX,"E92");
            var Q1;
            Q1=makeQuery(id+"F1.opExtrude","SWEPT_BODY",BODY,{"disambiguationData":[OSD([sQuery(id+"F0.wireOp",EDGE,"E0.bottom"),sQuery(id+"F0.wireOp",EDGE,"E0.top"),sQuery(id+"F0.wireOp",EDGE,"E0.left"),sQuery(id+"F0.wireOp",EDGE,"E0.right")])]});
            hole(context, id + "F42", {"style" : HoleStyle.SIMPLE, "endStyle" : HoleEndStyle.THROUGH, "holeDiameter" : 0.1 * mm, "startFromSketch" : true, "locations" : qUnion([Q0]), "scope" : qUnion([Q1]), "isTappedThrough" : true});
        }
        {
            var Q0;
            Q0=makeQuery(id+"F4.boolean.opBoolean","COPY",FACE,{"derivedFrom":makeQuery(id+"F4.opExtrude","CAP_FACE",FACE,{"disambiguationData":[OSD([sQuery(id+"F3.wireOp",EDGE,"E63.bottom"),sQuery(id+"F3.wireOp",EDGE,"E63.top"),sQuery(id+"F3.wireOp",EDGE,"E63.left"),sQuery(id+"F3.wireOp",EDGE,"E63.right")])],"isStart":false})});
            var sketch = newSketch(context, id + "F43", { "sketchPlane" : qUnion([Q0])});
            skPoint(sketch, "E93", {"position": v(-4.5, -2.5) * mm});
            skSolve(sketch);
        }
        {
            var Q0;
            Q0=sQuery(id+"F43.wireOp",VERTEX,"E93");
            var Q1;
            Q1=makeQuery(id+"F1.opExtrude","SWEPT_BODY",BODY,{"disambiguationData":[OSD([sQuery(id+"F0.wireOp",EDGE,"E0.bottom"),sQuery(id+"F0.wireOp",EDGE,"E0.top"),sQuery(id+"F0.wireOp",EDGE,"E0.left"),sQuery(id+"F0.wireOp",EDGE,"E0.right")])]});
            hole(context, id + "F44", {"style" : HoleStyle.SIMPLE, "endStyle" : HoleEndStyle.THROUGH, "holeDiameter" : 0.1 * mm, "startFromSketch" : true, "locations" : qUnion([Q0]), "scope" : qUnion([Q1]), "isTappedThrough" : true});
        }
        {
            var Q0;
            Q0=makeQuery(id+"F4.boolean.opBoolean","COPY",FACE,{"derivedFrom":makeQuery(id+"F4.opExtrude","CAP_FACE",FACE,{"disambiguationData":[OSD([sQuery(id+"F3.wireOp",EDGE,"E64.bottom"),sQuery(id+"F3.wireOp",EDGE,"E64.top"),sQuery(id+"F3.wireOp",EDGE,"E64.left"),sQuery(id+"F3.wireOp",EDGE,"E64.right")])],"isStart":false})});
            var sketch = newSketch(context, id + "F45", { "sketchPlane" : qUnion([Q0])});
            skPoint(sketch, "E94", {"position": v(-1.5, -2.5) * mm});
            skSolve(sketch);
        }
        {
            var Q0;
            Q0=sQuery(id+"F45.wireOp",VERTEX,"E94");
            var Q1;
            Q1=makeQuery(id+"F1.opExtrude","SWEPT_BODY",BODY,{"disambiguationData":[OSD([sQuery(id+"F0.wireOp",EDGE,"E0.bottom"),sQuery(id+"F0.wireOp",EDGE,"E0.top"),sQuery(id+"F0.wireOp",EDGE,"E0.left"),sQuery(id+"F0.wireOp",EDGE,"E0.right")])]});
            hole(context, id + "F46", {"style" : HoleStyle.SIMPLE, "endStyle" : HoleEndStyle.THROUGH, "holeDiameter" : 0.1 * mm, "startFromSketch" : true, "locations" : qUnion([Q0]), "scope" : qUnion([Q1]), "isTappedThrough" : true});
        }
        {
            var Q0;
            Q0=makeQuery(id+"F4.boolean.opBoolean","COPY",FACE,{"derivedFrom":makeQuery(id+"F4.opExtrude","CAP_FACE",FACE,{"disambiguationData":[OSD([sQuery(id+"F3.wireOp",EDGE,"E65.bottom"),sQuery(id+"F3.wireOp",EDGE,"E65.top"),sQuery(id+"F3.wireOp",EDGE,"E65.left"),sQuery(id+"F3.wireOp",EDGE,"E65.right")])],"isStart":false})});
            var sketch = newSketch(context, id + "F47", { "sketchPlane" : qUnion([Q0])});
            skPoint(sketch, "E95", {"position": v(1.5, -2.5) * mm});
            skSolve(sketch);
        }
        {
            var Q0;
            Q0=sQuery(id+"F47.wireOp",VERTEX,"E95");
            var Q1;
            Q1=makeQuery(id+"F1.opExtrude","SWEPT_BODY",BODY,{"disambiguationData":[OSD([sQuery(id+"F0.wireOp",EDGE,"E0.bottom"),sQuery(id+"F0.wireOp",EDGE,"E0.top"),sQuery(id+"F0.wireOp",EDGE,"E0.left"),sQuery(id+"F0.wireOp",EDGE,"E0.right")])]});
            hole(context, id + "F48", {"style" : HoleStyle.SIMPLE, "endStyle" : HoleEndStyle.THROUGH, "holeDiameter" : 0.1 * mm, "startFromSketch" : true, "locations" : qUnion([Q0]), "scope" : qUnion([Q1]), "isTappedThrough" : true});
        }
        {
            var Q0;
            Q0=makeQuery(id+"F4.boolean.opBoolean","COPY",FACE,{"derivedFrom":makeQuery(id+"F4.opExtrude","CAP_FACE",FACE,{"disambiguationData":[OSD([sQuery(id+"F3.wireOp",EDGE,"E66.bottom"),sQuery(id+"F3.wireOp",EDGE,"E66.top"),sQuery(id+"F3.wireOp",EDGE,"E66.left"),sQuery(id+"F3.wireOp",EDGE,"E66.right")])],"isStart":false})});
            var sketch = newSketch(context, id + "F49", { "sketchPlane" : qUnion([Q0])});
            skPoint(sketch, "E96", {"position": v(4.5, -2.5) * mm});
            skSolve(sketch);
        }
        {
            var Q0;
            Q0=sQuery(id+"F49.wireOp",VERTEX,"E96");
            var Q1;
            Q1=makeQuery(id+"F1.opExtrude","SWEPT_BODY",BODY,{"disambiguationData":[OSD([sQuery(id+"F0.wireOp",EDGE,"E0.bottom"),sQuery(id+"F0.wireOp",EDGE,"E0.top"),sQuery(id+"F0.wireOp",EDGE,"E0.left"),sQuery(id+"F0.wireOp",EDGE,"E0.right")])]});
            hole(context, id + "F50", {"style" : HoleStyle.SIMPLE, "endStyle" : HoleEndStyle.THROUGH, "holeDiameter" : 0.1 * mm, "startFromSketch" : true, "locations" : qUnion([Q0]), "scope" : qUnion([Q1]), "isTappedThrough" : true});
        }
        {
            var Q0;
            Q0=makeQuery(id+"F4.boolean.opBoolean","COPY",FACE,{"derivedFrom":makeQuery(id+"F4.opExtrude","CAP_FACE",FACE,{"disambiguationData":[OSD([sQuery(id+"F3.wireOp",EDGE,"E67.bottom"),sQuery(id+"F3.wireOp",EDGE,"E67.top"),sQuery(id+"F3.wireOp",EDGE,"E67.left"),sQuery(id+"F3.wireOp",EDGE,"E67.right")])],"isStart":false})});
            var sketch = newSketch(context, id + "F51", { "sketchPlane" : qUnion([Q0])});
            skPoint(sketch, "E97", {"position": v(7.5, -2.5) * mm});
            skSolve(sketch);
        }
        {
            var Q0;
            Q0=sQuery(id+"F51.wireOp",VERTEX,"E97");
            var Q1;
            Q1=makeQuery(id+"F1.opExtrude","SWEPT_BODY",BODY,{"disambiguationData":[OSD([sQuery(id+"F0.wireOp",EDGE,"E0.bottom"),sQuery(id+"F0.wireOp",EDGE,"E0.top"),sQuery(id+"F0.wireOp",EDGE,"E0.left"),sQuery(id+"F0.wireOp",EDGE,"E0.right")])]});
            hole(context, id + "F52", {"style" : HoleStyle.SIMPLE, "endStyle" : HoleEndStyle.THROUGH, "holeDiameter" : 0.1 * mm, "startFromSketch" : true, "locations" : qUnion([Q0]), "scope" : qUnion([Q1]), "isTappedThrough" : true});
        }
        {
            var Q0;
            Q0=makeQuery(id+"F4.boolean.opBoolean","COPY",FACE,{"derivedFrom":makeQuery(id+"F4.opExtrude","CAP_FACE",FACE,{"disambiguationData":[OSD([sQuery(id+"F3.wireOp",EDGE,"E73.bottom"),sQuery(id+"F3.wireOp",EDGE,"E73.top"),sQuery(id+"F3.wireOp",EDGE,"E73.left"),sQuery(id+"F3.wireOp",EDGE,"E73.right")])],"isStart":false})});
            var sketch = newSketch(context, id + "F53", { "sketchPlane" : qUnion([Q0])});
            skPoint(sketch, "E98", {"position": v(7.5, -5) * mm});
            skSolve(sketch);
        }
        {
            var Q0;
            Q0=sQuery(id+"F53.wireOp",VERTEX,"E98");
            var Q1;
            Q1=makeQuery(id+"F1.opExtrude","SWEPT_BODY",BODY,{"disambiguationData":[OSD([sQuery(id+"F0.wireOp",EDGE,"E0.bottom"),sQuery(id+"F0.wireOp",EDGE,"E0.top"),sQuery(id+"F0.wireOp",EDGE,"E0.left"),sQuery(id+"F0.wireOp",EDGE,"E0.right")])]});
            hole(context, id + "F54", {"style" : HoleStyle.SIMPLE, "endStyle" : HoleEndStyle.THROUGH, "holeDiameter" : 0.1 * mm, "startFromSketch" : true, "locations" : qUnion([Q0]), "scope" : qUnion([Q1]), "isTappedThrough" : true});
        }
        {
            var Q0;
            Q0=makeQuery(id+"F4.boolean.opBoolean","COPY",FACE,{"derivedFrom":makeQuery(id+"F4.opExtrude","CAP_FACE",FACE,{"disambiguationData":[OSD([sQuery(id+"F3.wireOp",EDGE,"E72.bottom"),sQuery(id+"F3.wireOp",EDGE,"E72.top"),sQuery(id+"F3.wireOp",EDGE,"E72.left"),sQuery(id+"F3.wireOp",EDGE,"E72.right")])],"isStart":false})});
            var sketch = newSketch(context, id + "F55", { "sketchPlane" : qUnion([Q0])});
            skPoint(sketch, "E99", {"position": v(4.5, -5) * mm});
            skSolve(sketch);
        }
        {
            var Q0;
            Q0=sQuery(id+"F55.wireOp",VERTEX,"E99");
            var Q1;
            Q1=makeQuery(id+"F1.opExtrude","SWEPT_BODY",BODY,{"disambiguationData":[OSD([sQuery(id+"F0.wireOp",EDGE,"E0.bottom"),sQuery(id+"F0.wireOp",EDGE,"E0.top"),sQuery(id+"F0.wireOp",EDGE,"E0.left"),sQuery(id+"F0.wireOp",EDGE,"E0.right")])]});
            hole(context, id + "F56", {"style" : HoleStyle.SIMPLE, "endStyle" : HoleEndStyle.THROUGH, "holeDiameter" : 0.1 * mm, "startFromSketch" : true, "locations" : qUnion([Q0]), "scope" : qUnion([Q1]), "isTappedThrough" : true});
        }
        {
            var Q0;
            Q0=makeQuery(id+"F4.boolean.opBoolean","COPY",FACE,{"derivedFrom":makeQuery(id+"F4.opExtrude","CAP_FACE",FACE,{"disambiguationData":[OSD([sQuery(id+"F3.wireOp",EDGE,"E71.bottom"),sQuery(id+"F3.wireOp",EDGE,"E71.top"),sQuery(id+"F3.wireOp",EDGE,"E71.left"),sQuery(id+"F3.wireOp",EDGE,"E71.right")])],"isStart":false})});
            var sketch = newSketch(context, id + "F57", { "sketchPlane" : qUnion([Q0])});
            skPoint(sketch, "E100", {"position": v(1.5, -5) * mm});
            skSolve(sketch);
        }
        {
            var Q0;
            Q0=sQuery(id+"F57.wireOp",VERTEX,"E100");
            var Q1;
            Q1=makeQuery(id+"F1.opExtrude","SWEPT_BODY",BODY,{"disambiguationData":[OSD([sQuery(id+"F0.wireOp",EDGE,"E0.bottom"),sQuery(id+"F0.wireOp",EDGE,"E0.top"),sQuery(id+"F0.wireOp",EDGE,"E0.left"),sQuery(id+"F0.wireOp",EDGE,"E0.right")])]});
            hole(context, id + "F58", {"style" : HoleStyle.SIMPLE, "endStyle" : HoleEndStyle.THROUGH, "holeDiameter" : 0.1 * mm, "startFromSketch" : true, "locations" : qUnion([Q0]), "scope" : qUnion([Q1]), "isTappedThrough" : true});
        }
        {
            var Q0;
            Q0=makeQuery(id+"F4.boolean.opBoolean","COPY",FACE,{"derivedFrom":makeQuery(id+"F4.opExtrude","CAP_FACE",FACE,{"disambiguationData":[OSD([sQuery(id+"F3.wireOp",EDGE,"E70.bottom"),sQuery(id+"F3.wireOp",EDGE,"E70.top"),sQuery(id+"F3.wireOp",EDGE,"E70.left"),sQuery(id+"F3.wireOp",EDGE,"E70.right")])],"isStart":false})});
            var sketch = newSketch(context, id + "F59", { "sketchPlane" : qUnion([Q0])});
            skPoint(sketch, "E101", {"position": v(-1.5, -5) * mm});
            skSolve(sketch);
        }
        {
            var Q0;
            Q0=sQuery(id+"F59.wireOp",VERTEX,"E101");
            var Q1;
            Q1=makeQuery(id+"F1.opExtrude","SWEPT_BODY",BODY,{"disambiguationData":[OSD([sQuery(id+"F0.wireOp",EDGE,"E0.bottom"),sQuery(id+"F0.wireOp",EDGE,"E0.top"),sQuery(id+"F0.wireOp",EDGE,"E0.left"),sQuery(id+"F0.wireOp",EDGE,"E0.right")])]});
            hole(context, id + "F60", {"style" : HoleStyle.SIMPLE, "endStyle" : HoleEndStyle.THROUGH, "holeDiameter" : 0.1 * mm, "startFromSketch" : true, "locations" : qUnion([Q0]), "scope" : qUnion([Q1]), "isTappedThrough" : true});
        }
        {
            var Q0;
            Q0=makeQuery(id+"F4.boolean.opBoolean","COPY",FACE,{"derivedFrom":makeQuery(id+"F4.opExtrude","CAP_FACE",FACE,{"disambiguationData":[OSD([sQuery(id+"F3.wireOp",EDGE,"E69.bottom"),sQuery(id+"F3.wireOp",EDGE,"E69.top"),sQuery(id+"F3.wireOp",EDGE,"E69.left"),sQuery(id+"F3.wireOp",EDGE,"E69.right")])],"isStart":false})});
            var sketch = newSketch(context, id + "F61", { "sketchPlane" : qUnion([Q0])});
            skPoint(sketch, "E102", {"position": v(-4.5, -5) * mm});
            skSolve(sketch);
        }
        {
            var Q0;
            Q0=sQuery(id+"F61.wireOp",VERTEX,"E102");
            var Q1;
            Q1=makeQuery(id+"F1.opExtrude","SWEPT_BODY",BODY,{"disambiguationData":[OSD([sQuery(id+"F0.wireOp",EDGE,"E0.bottom"),sQuery(id+"F0.wireOp",EDGE,"E0.top"),sQuery(id+"F0.wireOp",EDGE,"E0.left"),sQuery(id+"F0.wireOp",EDGE,"E0.right")])]});
            hole(context, id + "F62", {"style" : HoleStyle.SIMPLE, "endStyle" : HoleEndStyle.THROUGH, "holeDiameter" : 0.1 * mm, "startFromSketch" : true, "locations" : qUnion([Q0]), "scope" : qUnion([Q1]), "isTappedThrough" : true});
        }
        {
            var Q0;
            Q0=makeQuery(id+"F4.boolean.opBoolean","COPY",FACE,{"derivedFrom":makeQuery(id+"F4.opExtrude","CAP_FACE",FACE,{"disambiguationData":[OSD([sQuery(id+"F3.wireOp",EDGE,"E68.bottom"),sQuery(id+"F3.wireOp",EDGE,"E68.top"),sQuery(id+"F3.wireOp",EDGE,"E68.left"),sQuery(id+"F3.wireOp",EDGE,"E68.right")])],"isStart":false})});
            var sketch = newSketch(context, id + "F63", { "sketchPlane" : qUnion([Q0])});
            skPoint(sketch, "E103", {"position": v(-7.5, -5) * mm});
            skSolve(sketch);
        }
        {
            var Q0;
            Q0=sQuery(id+"F63.wireOp",VERTEX,"E103");
            var Q1;
            Q1=makeQuery(id+"F1.opExtrude","SWEPT_BODY",BODY,{"disambiguationData":[OSD([sQuery(id+"F0.wireOp",EDGE,"E0.bottom"),sQuery(id+"F0.wireOp",EDGE,"E0.top"),sQuery(id+"F0.wireOp",EDGE,"E0.left"),sQuery(id+"F0.wireOp",EDGE,"E0.right")])]});
            hole(context, id + "F64", {"style" : HoleStyle.SIMPLE, "endStyle" : HoleEndStyle.THROUGH, "holeDiameter" : 0.1 * mm, "startFromSketch" : true, "locations" : qUnion([Q0]), "scope" : qUnion([Q1]), "isTappedThrough" : true});
        }
        {
            var Q0;
            Q0=makeQuery(id+"F2.imprint","IMPRINT",FACE,{"disambiguationData":[TD([[makeQuery(id+"F2.imprint","IMPRINT",EDGE,{"derivedFrom":sQuery(id+"F2.wireOp",EDGE,"E7")}),-1.0]])]});
            extrude(context, id + "F65", {"entities" : qUnion([Q0]), "operationType" : NewBodyOperationType.ADD, "depth" : 0.5 * mm, "offsetDistance" : 25 * mm});
        }
    });
